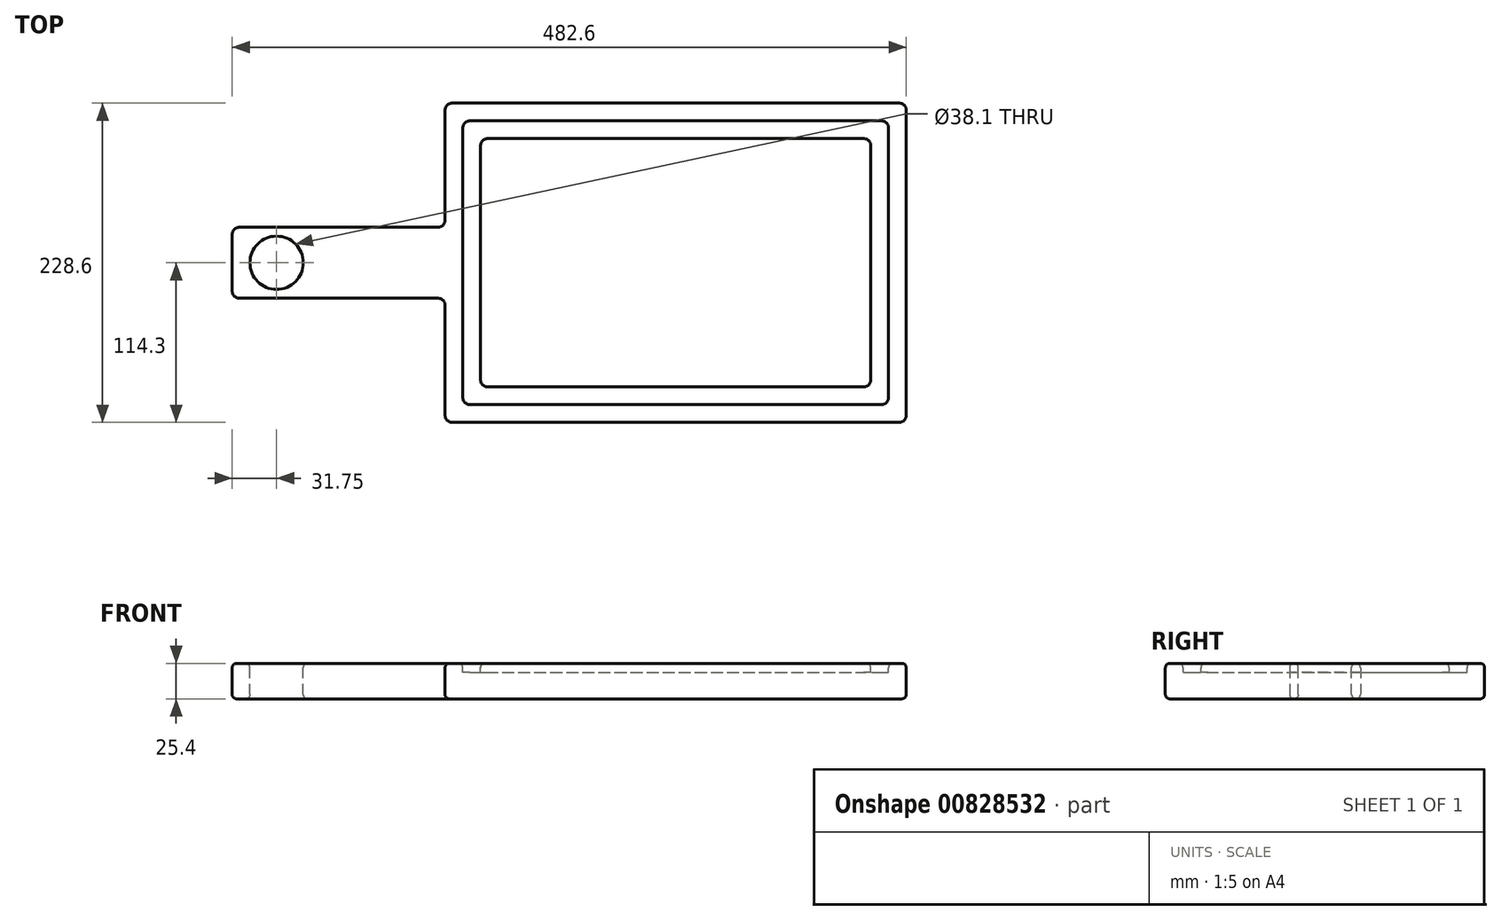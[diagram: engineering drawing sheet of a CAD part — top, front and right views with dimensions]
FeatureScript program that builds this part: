
annotation { "Feature Type Name" : "Feature", "Feature Type Description" : "" }
export const myFeature = defineFeature(function(context is Context, id is Id, definition is map)
    precondition{}
    {
        {
            var Q0;
            Q0=qCreatedBy(makeId("Top.planeOp"),FACE);
            var sketch = newSketch(context, id + "F0", { "sketchPlane" : qUnion([Q0])});
            skLineSegment(sketch, "E0.bottom", {"start": v(0, 0) * mm, "end": v(330.2, 0) * mm});
            skLineSegment(sketch, "E0.top", {"start": v(0, 228.6) * mm, "end": v(330.2, 228.6) * mm});
            skLineSegment(sketch, "E0.left", {"start": v(0, 0) * mm, "end": v(0, 228.6) * mm});
            skLineSegment(sketch, "E0.right", {"start": v(330.2, 0) * mm, "end": v(330.2, 228.6) * mm});
            skLineSegment(sketch, "E1.bottom", {"start": v(0, 139.7) * mm, "end": v(-152.4, 139.7) * mm});
            skLineSegment(sketch, "E1.top", {"start": v(0, 88.9) * mm, "end": v(-152.4, 88.9) * mm});
            skLineSegment(sketch, "E1.left", {"start": v(0, 139.7) * mm, "end": v(0, 88.9) * mm});
            skLineSegment(sketch, "E1.right", {"start": v(-152.4, 139.7) * mm, "end": v(-152.4, 88.9) * mm});
            skSolve(sketch);
        }
        {
            var Q0;
            {var subQ3=sQuery(id+"F0.wireOp",EDGE,"E0.bottom");Q0=makeQuery(id+"F0.imprint","IMPRINT",FACE,{"disambiguationData":[TD([[makeQuery(id+"F0.imprint","IMPRINT",EDGE,{"derivedFrom":subQ3}),1.0]])]});}
            var Q1;
            Q1=makeQuery(id+"F0.imprint","IMPRINT",FACE,{"disambiguationData":[TD([[makeQuery(id+"F0.imprint","IMPRINT",EDGE,{"derivedFrom":sQuery(id+"F0.wireOp",EDGE,"E1.bottom")}),1.0]])]});
            extrude(context, id + "F1", {"entities" : qUnion([Q0, Q1]), "depth" : 25.4 * mm, "offsetDistance" : 25.4 * mm});
        }
        {
            var Q0;
            Q0=makeQuery(id+"F1.opExtrude","CAP_FACE",FACE,{"disambiguationData":[OSD([sQuery(id+"F0.wireOp",EDGE,"E0.bottom"),sQuery(id+"F0.wireOp",EDGE,"E0.top"),sQuery(id+"F0.wireOp",EDGE,"E0.left"),sQuery(id+"F0.wireOp",EDGE,"E0.right"),sQuery(id+"F0.wireOp",EDGE,"E1.bottom"),sQuery(id+"F0.wireOp",EDGE,"E1.top"),sQuery(id+"F0.wireOp",EDGE,"E1.right")])],"isStart":false});
            var sketch = newSketch(context, id + "F2", { "sketchPlane" : qUnion([Q0])});
            skCircle(sketch, "E2", {"center": v(-120.65, 114.3) * mm, "radius": 19.05 * mm});
            skSolve(sketch);
        }
        {
            var Q0;
            Q0 = qSketchRegion(id + "F2", true);
            extrude(context, id + "F3", {"entities" : qUnion([Q0]), "operationType" : NewBodyOperationType.REMOVE, "oppositeDirection" : true, "depth" : 25.4 * mm, "offsetDistance" : 25.4 * mm});
        }
        {
            var Q0;
            Q0=makeQuery(id+"F1.opExtrude","CAP_FACE",FACE,{"disambiguationData":[OSD([sQuery(id+"F0.wireOp",EDGE,"E0.bottom"),sQuery(id+"F0.wireOp",EDGE,"E0.top"),sQuery(id+"F0.wireOp",EDGE,"E0.left"),sQuery(id+"F0.wireOp",EDGE,"E0.right"),sQuery(id+"F0.wireOp",EDGE,"E1.bottom"),sQuery(id+"F0.wireOp",EDGE,"E1.top"),sQuery(id+"F0.wireOp",EDGE,"E1.right")])],"isStart":false});
            var sketch = newSketch(context, id + "F4", { "sketchPlane" : qUnion([Q0])});
            skLineSegment(sketch, "E3.1", {"start": v(12.7, 139.7) * mm, "end": v(12.7, 215.9) * mm});
            skLineSegment(sketch, "E4.0", {"start": v(12.7, 12.7) * mm, "end": v(12.7, 88.9) * mm});
            skLineSegment(sketch, "E4.2", {"start": v(12.7, 215.9) * mm, "end": v(317.5, 215.9) * mm});
            skLineSegment(sketch, "E4.3", {"start": v(317.5, 12.7) * mm, "end": v(317.5, 215.9) * mm});
            skLineSegment(sketch, "E4.4", {"start": v(12.7, 12.7) * mm, "end": v(317.5, 12.7) * mm});
            skLineSegment(sketch, "E5.0", {"start": v(25.4, 25.4) * mm, "end": v(25.4, 88.9) * mm});
            skLineSegment(sketch, "E5.1", {"start": v(25.4, 25.4) * mm, "end": v(304.8, 25.4) * mm});
            skLineSegment(sketch, "E5.2", {"start": v(304.8, 25.4) * mm, "end": v(304.8, 203.2) * mm});
            skLineSegment(sketch, "E5.3", {"start": v(25.4, 203.2) * mm, "end": v(304.8, 203.2) * mm});
            skLineSegment(sketch, "E6.0", {"start": v(25.4, 139.7) * mm, "end": v(25.4, 203.2) * mm});
            skLineSegment(sketch, "E7", {"start": v(25.4, 139.7) * mm, "end": v(25.4, 88.9) * mm});
            skLineSegment(sketch, "E8", {"start": v(12.7, 139.7) * mm, "end": v(12.7, 88.9) * mm});
            skSolve(sketch);
        }
        {
            var Q0;
            Q0=makeQuery(id+"F4.imprint","IMPRINT",FACE,{"disambiguationData":[TD([[makeQuery(id+"F4.imprint","IMPRINT",EDGE,{"derivedFrom":sQuery(id+"F4.wireOp",EDGE,"E4.0")}),-1.0]])]});
            extrude(context, id + "F5", {"entities" : qUnion([Q0]), "operationType" : NewBodyOperationType.REMOVE, "oppositeDirection" : true, "depth" : 6.35 * mm, "offsetDistance" : 25.4 * mm});
        }
        {
            var Q0;
            Q0=makeQuery(id+"F5.boolean.opBoolean","COPY",EDGE,{"derivedFrom":makeQuery(id+"F5.opExtrude","SWEPT_EDGE",EDGE,{"disambiguationData":[OSD([sQuery(id+"F4.wireOp",EDGE,"E4.0"),sQuery(id+"F4.wireOp",EDGE,"E4.4")])]})});
            var Q1;
            Q1=makeQuery(id+"F5.boolean.opBoolean","COPY",EDGE,{"derivedFrom":makeQuery(id+"F5.opExtrude","SWEPT_EDGE",EDGE,{"disambiguationData":[OSD([sQuery(id+"F4.wireOp",EDGE,"E3.1"),sQuery(id+"F4.wireOp",EDGE,"E4.2")])]})});
            var Q2;
            Q2=makeQuery(id+"F5.boolean.opBoolean","COPY",EDGE,{"derivedFrom":makeQuery(id+"F5.opExtrude","SWEPT_EDGE",EDGE,{"disambiguationData":[OSD([sQuery(id+"F4.wireOp",EDGE,"E4.3"),sQuery(id+"F4.wireOp",EDGE,"E4.4")])]})});
            var Q3;
            Q3=makeQuery(id+"F5.boolean.opBoolean","COPY",EDGE,{"derivedFrom":makeQuery(id+"F5.opExtrude","SWEPT_EDGE",EDGE,{"disambiguationData":[OSD([sQuery(id+"F4.wireOp",EDGE,"E4.2"),sQuery(id+"F4.wireOp",EDGE,"E4.3")])]})});
            fillet(context, id + "F6", {"entities" : qUnion([Q0, Q1, Q2, Q3]), "radius" : 5.08 * mm, "tangentPropagation" : true, "allowEdgeOverflow" : false});
        }
        {
            var Q0;
            Q0=makeQuery(id+"F1.opExtrude","SWEPT_EDGE",EDGE,{"disambiguationData":[OSD([sQuery(id+"F0.wireOp",EDGE,"E0.top"),sQuery(id+"F0.wireOp",EDGE,"E0.left")])]});
            var Q1;
            Q1=makeQuery(id+"F1.opExtrude","SWEPT_EDGE",EDGE,{"disambiguationData":[OSD([sQuery(id+"F0.wireOp",EDGE,"E0.bottom"),sQuery(id+"F0.wireOp",EDGE,"E0.left")])]});
            var Q2;
            Q2=makeQuery(id+"F1.opExtrude","SWEPT_EDGE",EDGE,{"disambiguationData":[OSD([sQuery(id+"F0.wireOp",EDGE,"E1.top"),sQuery(id+"F0.wireOp",EDGE,"E1.right")])]});
            var Q3;
            Q3=makeQuery(id+"F1.opExtrude","SWEPT_EDGE",EDGE,{"disambiguationData":[OSD([sQuery(id+"F0.wireOp",EDGE,"E1.bottom"),sQuery(id+"F0.wireOp",EDGE,"E1.right")])]});
            var Q4;
            Q4=makeQuery(id+"F1.opExtrude","SWEPT_EDGE",EDGE,{"disambiguationData":[OSD([sQuery(id+"F0.wireOp",EDGE,"E0.left"),sQuery(id+"F0.wireOp",EDGE,"E1.bottom"),sQuery(id+"F0.wireOp",EDGE,"E1.left")])]});
            var Q5;
            Q5=makeQuery(id+"F1.opExtrude","SWEPT_EDGE",EDGE,{"disambiguationData":[OSD([sQuery(id+"F0.wireOp",EDGE,"E0.left"),sQuery(id+"F0.wireOp",EDGE,"E1.top"),sQuery(id+"F0.wireOp",EDGE,"E1.left")])]});
            var Q6;
            Q6=makeQuery(id+"F1.opExtrude","SWEPT_EDGE",EDGE,{"disambiguationData":[OSD([sQuery(id+"F0.wireOp",EDGE,"E0.bottom"),sQuery(id+"F0.wireOp",EDGE,"E0.right")])]});
            var Q7;
            Q7=makeQuery(id+"F1.opExtrude","SWEPT_EDGE",EDGE,{"disambiguationData":[OSD([sQuery(id+"F0.wireOp",EDGE,"E0.top"),sQuery(id+"F0.wireOp",EDGE,"E0.right")])]});
            fillet(context, id + "F7", {"entities" : qUnion([Q0, Q1, Q2, Q3, Q4, Q5, Q6, Q7]), "radius" : 5.08 * mm, "tangentPropagation" : true, "allowEdgeOverflow" : false});
        }
        {
            var Q0;
            Q0=makeQuery(id+"F5.boolean.opBoolean","COPY",EDGE,{"derivedFrom":makeQuery(id+"F5.opExtrude","SWEPT_EDGE",EDGE,{"disambiguationData":[OSD([sQuery(id+"F4.wireOp",EDGE,"E5.3"),sQuery(id+"F4.wireOp",EDGE,"E6.0")])]})});
            var Q1;
            Q1=makeQuery(id+"F5.boolean.opBoolean","COPY",EDGE,{"derivedFrom":makeQuery(id+"F5.opExtrude","SWEPT_EDGE",EDGE,{"disambiguationData":[OSD([sQuery(id+"F4.wireOp",EDGE,"E5.0"),sQuery(id+"F4.wireOp",EDGE,"E5.1")])]})});
            var Q2;
            Q2=makeQuery(id+"F5.boolean.opBoolean","COPY",EDGE,{"derivedFrom":makeQuery(id+"F5.opExtrude","SWEPT_EDGE",EDGE,{"disambiguationData":[OSD([sQuery(id+"F4.wireOp",EDGE,"E5.1"),sQuery(id+"F4.wireOp",EDGE,"E5.2")])]})});
            var Q3;
            Q3=makeQuery(id+"F5.boolean.opBoolean","COPY",EDGE,{"derivedFrom":makeQuery(id+"F5.opExtrude","SWEPT_EDGE",EDGE,{"disambiguationData":[OSD([sQuery(id+"F4.wireOp",EDGE,"E5.2"),sQuery(id+"F4.wireOp",EDGE,"E5.3")])]})});
            fillet(context, id + "F8", {"entities" : qUnion([Q0, Q1, Q2, Q3]), "radius" : 5.08 * mm, "tangentPropagation" : true, "allowEdgeOverflow" : false});
        }
        {
            var Q0;
            {var subQ0=sQuery(id+"F0.wireOp",EDGE,"E1.right");var subQ1=sQuery(id+"F0.wireOp",EDGE,"E1.top");var subQ2=sQuery(id+"F0.wireOp",EDGE,"E1.bottom");var subQ3=sQuery(id+"F0.wireOp",EDGE,"E0.right");var subQ4=sQuery(id+"F0.wireOp",EDGE,"E0.bottom");var subQ5=sQuery(id+"F0.wireOp",EDGE,"E0.left");var subQ6=sQuery(id+"F0.wireOp",EDGE,"E0.top");Q0=makeQuery(id+"F5.boolean.opBoolean","SPLIT",FACE,{"disambiguationData":[TD([makeQuery(id+"F1.opExtrude","SWEPT_FACE",FACE,{"disambiguationData":[OSD([subQ4])]})])],"derivedFrom":makeQuery(id+"F1.opExtrude","CAP_FACE",FACE,{"disambiguationData":[OSD([subQ4,subQ6,subQ5,subQ3,subQ2,subQ1,subQ0])],"isStart":false})});}
            var Q1;
            Q1=makeQuery(id+"F5.boolean.opBoolean","SPLIT",FACE,{"disambiguationData":[TD([makeQuery(id+"F5.opExtrude","SWEPT_FACE",FACE,{"disambiguationData":[OSD([sQuery(id+"F4.wireOp",EDGE,"E5.0")])]})])],"derivedFrom":makeQuery(id+"F1.opExtrude","CAP_FACE",FACE,{"disambiguationData":[OSD([sQuery(id+"F0.wireOp",EDGE,"E0.bottom"),sQuery(id+"F0.wireOp",EDGE,"E0.top"),sQuery(id+"F0.wireOp",EDGE,"E0.left"),sQuery(id+"F0.wireOp",EDGE,"E0.right"),sQuery(id+"F0.wireOp",EDGE,"E1.bottom"),sQuery(id+"F0.wireOp",EDGE,"E1.top"),sQuery(id+"F0.wireOp",EDGE,"E1.right")])],"isStart":false})});
            var Q2;
            Q2=makeQuery(id+"F1.opExtrude","CAP_FACE",FACE,{"disambiguationData":[OSD([sQuery(id+"F0.wireOp",EDGE,"E0.bottom"),sQuery(id+"F0.wireOp",EDGE,"E0.top"),sQuery(id+"F0.wireOp",EDGE,"E0.left"),sQuery(id+"F0.wireOp",EDGE,"E0.right"),sQuery(id+"F0.wireOp",EDGE,"E1.bottom"),sQuery(id+"F0.wireOp",EDGE,"E1.top"),sQuery(id+"F0.wireOp",EDGE,"E1.right")])],"isStart":true});
            fillet(context, id + "F9", {"entities" : qUnion([Q0, Q1, Q2]), "radius" : 3.17 * mm, "tangentPropagation" : true, "allowEdgeOverflow" : false});
        }
    });
